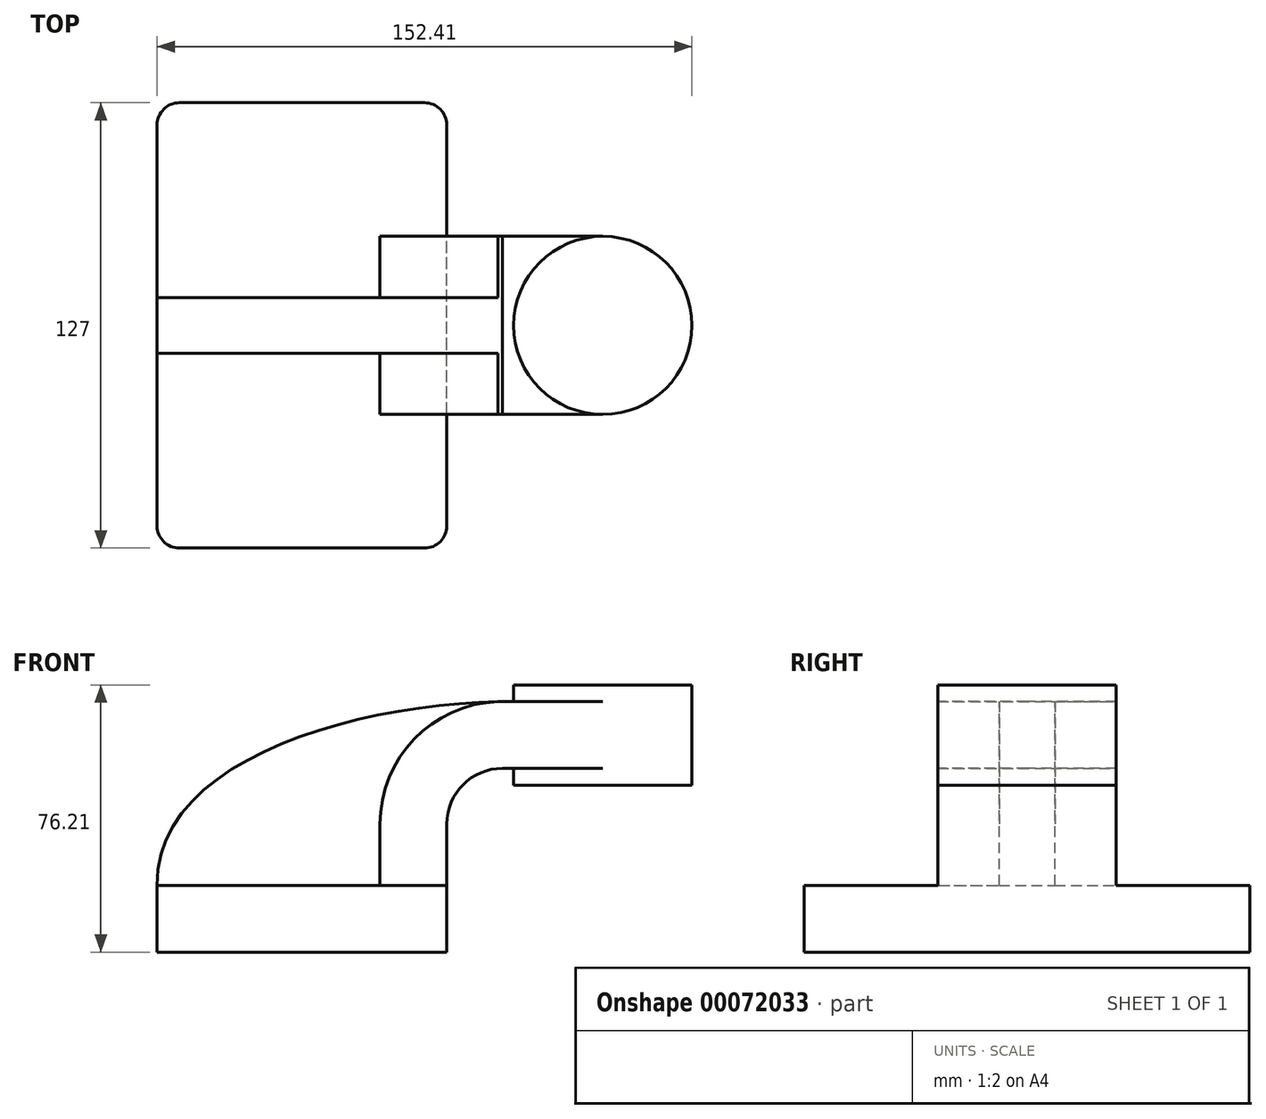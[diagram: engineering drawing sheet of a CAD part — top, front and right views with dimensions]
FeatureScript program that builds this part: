
annotation { "Feature Type Name" : "Feature", "Feature Type Description" : "" }
export const myFeature = defineFeature(function(context is Context, id is Id, definition is map)
    precondition{}
    {
        {
            var Q0;
            Q0=qCreatedBy(makeId("Front.planeOp"),FACE);
            var sketch = newSketch(context, id + "F0", { "sketchPlane" : qUnion([Q0])});
            skLineSegment(sketch, "E0.rect.bottom", {"start": v(-41.28, -9.53) * mm, "end": v(41.28, -9.53) * mm});
            skLineSegment(sketch, "E0.rect.top", {"start": v(-41.28, 9.53) * mm, "end": v(41.28, 9.53) * mm});
            skLineSegment(sketch, "E0.rect.left", {"start": v(-41.28, -9.53) * mm, "end": v(-41.28, 9.53) * mm});
            skLineSegment(sketch, "E0.rect.right", {"start": v(41.28, -9.53) * mm, "end": v(41.28, 9.53) * mm});
            skPoint(sketch, "E0.rect.middle", {"position": v(0, 0) * mm});
            skLineSegment(sketch, "E1.rect.bottom", {"start": v(60.32, 66.68) * mm, "end": v(111.12, 66.68) * mm});
            skLineSegment(sketch, "E1.rect.top", {"start": v(60.32, 38.1) * mm, "end": v(111.12, 38.1) * mm});
            skLineSegment(sketch, "E1.rect.left", {"start": v(60.32, 66.68) * mm, "end": v(60.32, 38.1) * mm});
            skLineSegment(sketch, "E1.rect.right", {"start": v(111.12, 66.68) * mm, "end": v(111.12, 38.1) * mm});
            skPoint(sketch, "E1.rect.middle", {"position": v(85.72, 52.39) * mm});
            skLineSegment(sketch, "E2", {"start": v(41.28, 9.53) * mm, "end": v(41.28, 27) * mm});
            skArc(sketch, "E3", {"start": v(41.27, 27) * mm, "mid": v(45.92, 38.23) * mm, "end": v(57.15, 42.88) * mm});
            skLineSegment(sketch, "E4", {"start": v(57.15, 42.88) * mm, "end": v(85.72, 42.88) * mm});
            skLineSegment(sketch, "E5.0", {"start": v(57.15, 61.93) * mm, "end": v(85.72, 61.93) * mm});
            skArc(sketch, "E5.1", {"start": v(22.23, 27) * mm, "mid": v(32.45, 51.7) * mm, "end": v(57.15, 61.93) * mm});
            skLineSegment(sketch, "E5.2", {"start": v(22.23, 9.53) * mm, "end": v(22.23, 27) * mm});
            skLineSegment(sketch, "E6", {"start": v(85.72, 38.1) * mm, "end": v(85.72, 66.68) * mm});
            skFitSpline(sketch, "E7", {"points": [v(-41.28, 9.52) * mm, v(57.15, 61.93) * mm], "startDerivative": vector(-1.41, 108.24) * mm, "endDerivative": vector(124.2, 1.86) * mm});
            skSolve(sketch);
        }
        {
            var Q0;
            Q0=makeQuery(id+"F0.imprint","IMPRINT",FACE,{"disambiguationData":[TD([[makeQuery(id+"F0.imprint","IMPRINT",EDGE,{"derivedFrom":sQuery(id+"F0.wireOp",EDGE,"E0.rect.bottom")}),1.0]])]});
            extrude(context, id + "F1", {"entities" : qUnion([Q0]), "depth" : 127 * mm, "symmetric" : true});
        }
        {
            var Q0;
            {var subQ1=sQuery(id+"F0.wireOp",EDGE,"E2");Q0=makeQuery(id+"F0.imprint","IMPRINT",FACE,{"disambiguationData":[TD([[makeQuery(id+"F0.imprint","IMPRINT",EDGE,{"derivedFrom":subQ1}),1.0]])]});}
            var Q1;
            {var subQ0=sQuery(id+"F0.wireOp",EDGE,"E5.0");var subQ1=sQuery(id+"F0.wireOp",EDGE,"E1.rect.left");var subQ2=makeQuery(id+"F0.imprint","INTERSECT",VERTEX,{"derivedFrom":[subQ1,subQ0]});Q1=makeQuery(id+"F0.imprint","IMPRINT",FACE,{"disambiguationData":[TD([[makeQuery(id+"F0.imprint","IMPRINT",EDGE,{"disambiguationData":[TD([[subQ2,-1.0]])],"derivedFrom":subQ1}),1.0]])]});}
            extrude(context, id + "F2", {"entities" : qUnion([Q0, Q1]), "operationType" : NewBodyOperationType.ADD, "depth" : 50.8 * mm, "symmetric" : true});
        }
        {
            var Q0;
            {var subQ3=sQuery(id+"F0.wireOp",EDGE,"E5.2");Q0=makeQuery(id+"F0.imprint","IMPRINT",FACE,{"disambiguationData":[TD([[makeQuery(id+"F0.imprint","IMPRINT",EDGE,{"derivedFrom":subQ3}),1.0]])]});}
            extrude(context, id + "F3", {"entities" : qUnion([Q0]), "operationType" : NewBodyOperationType.ADD, "depth" : 15.88 * mm, "symmetric" : true});
        }
        {
            var Q0;
            {var subQ0=sQuery(id+"F0.wireOp",EDGE,"E1.rect.right");Q0=makeQuery(id+"F0.imprint","IMPRINT",FACE,{"disambiguationData":[TD([[makeQuery(id+"F0.imprint","IMPRINT",EDGE,{"derivedFrom":subQ0}),-1.0]])]});}
            var Q1;
            Q1=sQuery(id+"F0.wireOp",EDGE,"E6");
            revolve(context, id + "F4", {"operationType" : NewBodyOperationType.ADD, "entities" : qUnion([Q0]), "axis" : qUnion([Q1]), "revolveType" : RevolveType.FULL});
        }
        {
            var Q0;
            Q0=makeQuery(id+"F1.opExtrude","CAP_EDGE",EDGE,{"disambiguationData":[OSD([sQuery(id+"F0.wireOp",EDGE,"E0.rect.right")])],"isStart":false});
            var Q1;
            Q1=makeQuery(id+"F1.opExtrude","CAP_EDGE",EDGE,{"disambiguationData":[OSD([sQuery(id+"F0.wireOp",EDGE,"E0.rect.left")])],"isStart":false});
            var Q2;
            Q2=makeQuery(id+"F1.opExtrude","CAP_EDGE",EDGE,{"disambiguationData":[OSD([sQuery(id+"F0.wireOp",EDGE,"E0.rect.right")])],"isStart":true});
            var Q3;
            Q3=makeQuery(id+"F1.opExtrude","CAP_EDGE",EDGE,{"disambiguationData":[OSD([sQuery(id+"F0.wireOp",EDGE,"E0.rect.left")])],"isStart":true});
            fillet(context, id + "F5", {"entities" : qUnion([Q0, Q1, Q2, Q3]), "radius" : 6.35 * mm, "tangentPropagation" : true, "allowEdgeOverflow" : false});
        }
    });
